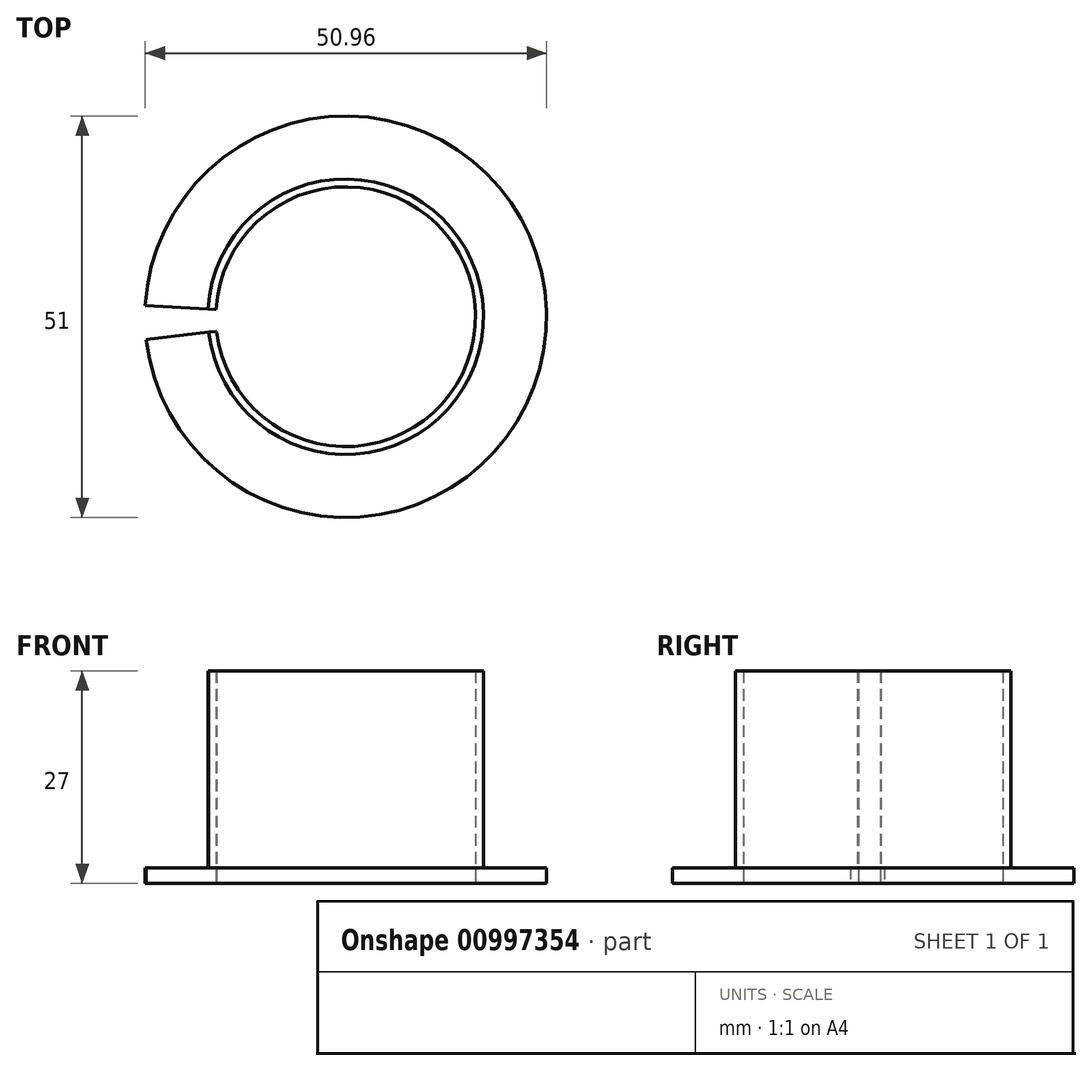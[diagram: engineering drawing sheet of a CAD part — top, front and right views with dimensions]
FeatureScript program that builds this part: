
annotation { "Feature Type Name" : "Feature", "Feature Type Description" : "" }
export const myFeature = defineFeature(function(context is Context, id is Id, definition is map)
    precondition{}
    {
        {
            var Q0;
            Q0=qCreatedBy(makeId("Top.planeOp"),FACE);
            var sketch = newSketch(context, id + "F0", { "sketchPlane" : qUnion([Q0])});
            skArc(sketch, "E0", {"start": v(-16.4, -1.86) * mm, "mid": v(16.5, 0.47) * mm, "end": v(-16.47, 0.93) * mm});
            skArc(sketch, "E1", {"start": v(-17.39, -1.97) * mm, "mid": v(17.5, 0.5) * mm, "end": v(-17.47, 0.98) * mm});
            skArc(sketch, "E2", {"start": v(-25.34, -2.87) * mm, "mid": v(25.49, 0.72) * mm, "end": v(-25.46, 1.43) * mm});
            skLineSegment(sketch, "E3", {"start": v(-25.34, -2.87) * mm, "end": v(0, 0) * mm});
            skLineSegment(sketch, "E4", {"start": v(-25.46, 1.43) * mm, "end": v(0, 0) * mm});
            skSolve(sketch);
        }
        {
            var Q0;
            Q0=makeQuery(id+"F0.imprint","IMPRINT",FACE,{"disambiguationData":[TD([[makeQuery(id+"F0.imprint","IMPRINT",EDGE,{"derivedFrom":sQuery(id+"F0.wireOp",EDGE,"E0")}),-1.0]])]});
            extrude(context, id + "F1", {"entities" : qUnion([Q0]), "depth" : 27 * mm, "offsetDistance" : 25 * mm});
        }
        {
            var Q0;
            Q0=makeQuery(id+"F0.imprint","IMPRINT",FACE,{"disambiguationData":[TD([[makeQuery(id+"F0.imprint","IMPRINT",EDGE,{"derivedFrom":sQuery(id+"F0.wireOp",EDGE,"E1")}),-1.0]])]});
            extrude(context, id + "F2", {"entities" : qUnion([Q0]), "operationType" : NewBodyOperationType.ADD, "depth" : 2 * mm, "offsetDistance" : 25 * mm});
        }
    });
